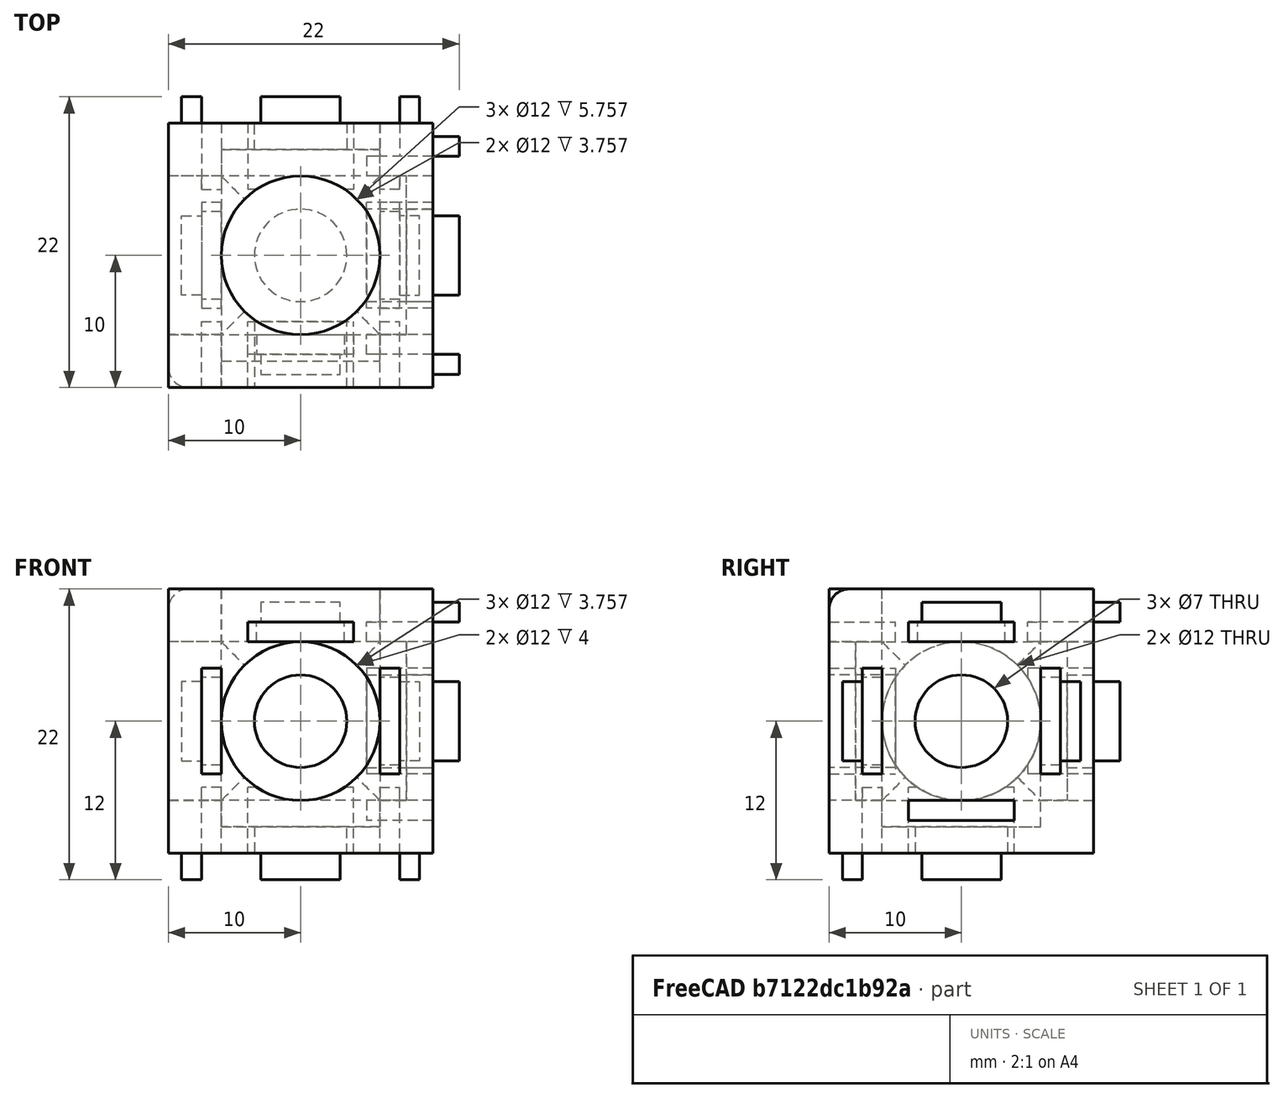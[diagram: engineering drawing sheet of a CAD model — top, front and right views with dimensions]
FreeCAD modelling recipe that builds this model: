
FCSTD DOCUMENT  (FreeCAD 0.15R4477 (Git))
Label: Wuerfelverbinder-20x20
License: CC-BY 3.0
LicenseURL: http://creativecommons.org/licenses/by/3.0/
objects: Sketcher::SketchObject×10, PartDesign::Pocket×6, PartDesign::Pad×4, PartDesign::Fillet×1
note: 31 computed .brp shape members not serialized (recipe doc carries the construction recipe); baked Part::Feature solids carry a one-line shape summary decoded from their .brp

FEATURE [Sketcher::SketchObject] Sketch
  Placement = pos=(0,0,0) rot=(1,0,0;1.5708rad)
  sketch-geometry (4):
    g0: LineSegment StartX=-10 StartY=10 StartZ=0 EndX=10 EndY=10 EndZ=0
    g1: LineSegment StartX=10 StartY=10 StartZ=0 EndX=10 EndY=-10 EndZ=0
    g2: LineSegment StartX=10 StartY=-10 StartZ=0 EndX=-10 EndY=-10 EndZ=0
    g3: LineSegment StartX=-10 StartY=-10 StartZ=0 EndX=-10 EndY=10 EndZ=0
  constraints (12):
    c: Coincident(g0,g1)
    c: Coincident(g1,g2)
    c: Coincident(g2,g3)
    c: Coincident(g3,g0)
    c: Horizontal(g0)
    c: Horizontal(g2)
    c: Vertical(g1)
    c: Vertical(g3)
    c: Symmetric(g0,g0,g-2)
    c: Symmetric(g2,g0,g-1)
    c: Distance(g0) = 20
    c: Distance(g1) = 20
FEATURE [PartDesign::Pad] Pad
  Length = 20
  Length2 = 100
  Midplane = true
  Placement = pos=(0,0,0) rot=(1,0,0;1.5708rad)
  Sketch = -> Sketch
  Type = 0
FEATURE [Sketcher::SketchObject] Sketch001
  Placement = pos=(0,-10,0) rot=(1,0,0;1.5708rad)
  Support = -> Pad [Face6]
  sketch-geometry (1):
    g0: Circle CenterX=0 CenterY=0 CenterZ=0 NormalX=0 NormalY=0 NormalZ=1 Radius=6
  constraints (2):
    c: Coincident(g0,g-1)
    c: Radius(g0) = 6
FEATURE [PartDesign::Pocket] Pocket
  Length = 18
  Placement = pos=(0,0,0) rot=(1,0,0;1.5708rad)
  Sketch = -> Sketch001
  Type = 0
FEATURE [Sketcher::SketchObject] Sketch003
  Placement = pos=(0,0,10) rot=(0,0,1;3.14159rad)
  Support = -> Pocket [Face1]
  sketch-geometry (1):
    g0: Circle CenterX=0 CenterY=0 CenterZ=0 NormalX=0 NormalY=0 NormalZ=1 Radius=6
  constraints (2):
    c: Coincident(g0,g-1)
    c: Radius(g0) = 6
FEATURE [PartDesign::Pocket] Pocket001
  Length = 18
  Placement = pos=(0,0,0) rot=(1,0,0;1.5708rad)
  Sketch = -> Sketch003
  Type = 0
FEATURE [Sketcher::SketchObject] Sketch004
  Placement = pos=(-10,0,0) rot=(0.707107,0,-0.707107;3.14159rad)
  Support = -> Pocket001 [Face2]
  sketch-geometry (1):
    g0: Circle CenterX=0 CenterY=0 CenterZ=0 NormalX=0 NormalY=0 NormalZ=1 Radius=6
  constraints (2):
    c: Coincident(g0,g-1)
    c: Radius(g0) = 6
FEATURE [PartDesign::Pocket] Pocket002
  Length = 18
  Placement = pos=(0,0,0) rot=(1,0,0;1.5708rad)
  Sketch = -> Sketch004
  Type = 0
FEATURE [Sketcher::SketchObject] Sketch005
  ExternalGeometry = -> [Pocket002]
  Placement = pos=(10,0,0) rot=(0.707107,0,0.707107;3.14159rad)
  Support = -> Pocket002 [Face5]
  sketch-geometry (12):
    g0: LineSegment StartX=7.5 StartY=3 StartZ=0 EndX=9 EndY=3 EndZ=0
    g1: LineSegment StartX=9 StartY=3 StartZ=0 EndX=9 EndY=-3 EndZ=0
    g2: LineSegment StartX=9 StartY=-3 StartZ=0 EndX=7.5 EndY=-3 EndZ=0
    g3: LineSegment StartX=7.5 StartY=-3 StartZ=0 EndX=7.5 EndY=3 EndZ=0
    g4: LineSegment StartX=3 StartY=9 StartZ=0 EndX=-3 EndY=9 EndZ=0
    g5: LineSegment StartX=-3 StartY=9 StartZ=0 EndX=-3 EndY=7.5 EndZ=0
    g6: LineSegment StartX=-3 StartY=7.5 StartZ=0 EndX=3 EndY=7.5 EndZ=0
    g7: LineSegment StartX=3 StartY=7.5 StartZ=0 EndX=3 EndY=9 EndZ=0
    g8: LineSegment StartX=3 StartY=-7.5 StartZ=0 EndX=-3 EndY=-7.5 EndZ=0
    g9: LineSegment StartX=-3 StartY=-7.5 StartZ=0 EndX=-3 EndY=-9 EndZ=0
    g10: LineSegment StartX=-3 StartY=-9 StartZ=0 EndX=3 EndY=-9 EndZ=0
    g11: LineSegment StartX=3 StartY=-9 StartZ=0 EndX=3 EndY=-7.5 EndZ=0
  constraints (36):
    c: Coincident(g0,g1)
    c: Coincident(g1,g2)
    c: Coincident(g2,g3)
    c: Coincident(g3,g0)
    c: Horizontal(g0)
    c: Horizontal(g2)
    c: Vertical(g1)
    c: Vertical(g3)
    c: Coincident(g4,g5)
    c: Coincident(g5,g6)
    c: Coincident(g6,g7)
    c: Coincident(g7,g4)
    c: Horizontal(g4)
    c: Horizontal(g6)
    c: Vertical(g5)
    c: Vertical(g7)
    c: Coincident(g8,g9)
    c: Coincident(g9,g10)
    c: Coincident(g10,g11)
    c: Coincident(g11,g8)
    c: Horizontal(g8)
    c: Horizontal(g10)
    c: Vertical(g9)
    c: Vertical(g11)
    c: Symmetric(g0,g1,g-1)
    c: Symmetric(g4,g4,g-2)
    c: Symmetric(g8,g8,g-2)
    c: Distance(g6) = 6
    c: Distance(g3) = 6
    c: Distance(g8) = 6
    c: Distance(g0,g-3) = 1
    c: Distance(g4,g-4) = 1
    c: Distance(g10,g-5) = 1
    c: Distance(g0) = 1.5
    c: Distance(g7) = 1.5
    c: Distance(g11) = 1.5
FEATURE [PartDesign::Pad] Pad001
  Length = 2
  Length2 = 100
  Placement = pos=(0,0,0) rot=(1,0,0;1.5708rad)
  Sketch = -> Sketch005
  Type = 0
FEATURE [Sketcher::SketchObject] Sketch006
  ExternalGeometry = -> [Pad001]
  Placement = pos=(10,0,0) rot=(0.707107,0,0.707107;3.14159rad)
  Support = -> Pad001 [Face5]
  sketch-geometry (13):
    g0: LineSegment StartX=-4 StartY=6 StartZ=0 EndX=4 EndY=6 EndZ=0
    g1: LineSegment StartX=4 StartY=6 StartZ=0 EndX=4 EndY=7.5 EndZ=0
    g2: LineSegment StartX=4 StartY=7.5 StartZ=0 EndX=-4 EndY=7.5 EndZ=0
    g3: LineSegment StartX=-4 StartY=7.5 StartZ=0 EndX=-4 EndY=6 EndZ=0
    g4: LineSegment StartX=6 StartY=4 StartZ=0 EndX=7.5 EndY=4 EndZ=0
    g5: LineSegment StartX=7.5 StartY=4 StartZ=0 EndX=7.5 EndY=-4 EndZ=0
    g6: LineSegment StartX=7.5 StartY=-4 StartZ=0 EndX=6 EndY=-4 EndZ=0
    g7: LineSegment StartX=6 StartY=-4 StartZ=0 EndX=6 EndY=4 EndZ=0
    g8: LineSegment StartX=-4 StartY=-6 StartZ=0 EndX=4 EndY=-6 EndZ=0
    g9: LineSegment StartX=4 StartY=-6 StartZ=0 EndX=4 EndY=-7.5 EndZ=0
    g10: LineSegment StartX=4 StartY=-7.5 StartZ=0 EndX=-4 EndY=-7.5 EndZ=0
    g11: LineSegment StartX=-4 StartY=-7.5 StartZ=0 EndX=-4 EndY=-6 EndZ=0
    g12: Circle CenterX=0 CenterY=0 CenterZ=0 NormalX=0 NormalY=0 NormalZ=1 Radius=3.5
  constraints (38):
    c: Coincident(g0,g1)
    c: Coincident(g1,g2)
    c: Coincident(g2,g3)
    c: Coincident(g3,g0)
    c: Horizontal(g0)
    c: Horizontal(g2)
    c: Vertical(g1)
    c: Vertical(g3)
    c: Coincident(g4,g5)
    c: Coincident(g5,g6)
    c: Coincident(g6,g7)
    c: Coincident(g7,g4)
    c: Horizontal(g4)
    c: Horizontal(g6)
    c: Vertical(g5)
    c: Vertical(g7)
    c: Coincident(g8,g9)
    c: Coincident(g9,g10)
    c: Coincident(g10,g11)
    c: Coincident(g11,g8)
    c: Horizontal(g8)
    c: Horizontal(g10)
    c: Vertical(g9)
    c: Vertical(g11)
    c: Symmetric(g2,g1,g-2)
    c: Symmetric(g4,g6,g-1)
    c: Symmetric(g8,g8,g-2)
    c: Distance(g3) = 1.5
    c: Distance(g4) = 1.5
    c: Distance(g11) = 1.5
    c: Distance(g8) = 8
    c: Distance(g7) = 8
    c: Distance(g0) = 8
    c: PointOnObject(g-5,g10)
    c: PointOnObject(g-4,g5)
    c: PointOnObject(g-3,g2)
    c: Coincident(g12,g-1)
    c: Radius(g12) = 3.5
FEATURE [PartDesign::Pocket] Pocket003
  Length = 5
  Placement = pos=(0,0,0) rot=(1,0,0;1.5708rad)
  Sketch = -> Sketch006
  Type = 0
FEATURE [Sketcher::SketchObject] Sketch007
  ExternalGeometry = -> [Pocket003]
  Placement = pos=(0,0,-10) rot=(1,0,0;3.14159rad)
  Support = -> Pocket003 [Face7]
  sketch-geometry (12):
    g0: LineSegment StartX=-3 StartY=9 StartZ=0 EndX=3 EndY=9 EndZ=0
    g1: LineSegment StartX=3 StartY=9 StartZ=0 EndX=3 EndY=7.5 EndZ=0
    g2: LineSegment StartX=3 StartY=7.5 StartZ=0 EndX=-3 EndY=7.5 EndZ=0
    g3: LineSegment StartX=-3 StartY=7.5 StartZ=0 EndX=-3 EndY=9 EndZ=0
    g4: LineSegment StartX=-7.5 StartY=3 StartZ=0 EndX=-9 EndY=3 EndZ=0
    g5: LineSegment StartX=-9 StartY=3 StartZ=0 EndX=-9 EndY=-3 EndZ=0
    g6: LineSegment StartX=-9 StartY=-3 StartZ=0 EndX=-7.5 EndY=-3 EndZ=0
    g7: LineSegment StartX=-7.5 StartY=-3 StartZ=0 EndX=-7.5 EndY=3 EndZ=0
    g8: LineSegment StartX=7.5 StartY=3 StartZ=0 EndX=9 EndY=3 EndZ=0
    g9: LineSegment StartX=9 StartY=3 StartZ=0 EndX=9 EndY=-3 EndZ=0
    g10: LineSegment StartX=9 StartY=-3 StartZ=0 EndX=7.5 EndY=-3 EndZ=0
    g11: LineSegment StartX=7.5 StartY=-3 StartZ=0 EndX=7.5 EndY=3 EndZ=0
  constraints (36):
    c: Coincident(g0,g1)
    c: Coincident(g1,g2)
    c: Coincident(g2,g3)
    c: Coincident(g3,g0)
    c: Horizontal(g0)
    c: Horizontal(g2)
    c: Vertical(g1)
    c: Vertical(g3)
    c: Coincident(g4,g5)
    c: Coincident(g5,g6)
    c: Coincident(g6,g7)
    c: Coincident(g7,g4)
    c: Horizontal(g4)
    c: Horizontal(g6)
    c: Vertical(g5)
    c: Vertical(g7)
    c: Coincident(g8,g9)
    c: Coincident(g9,g10)
    c: Coincident(g10,g11)
    c: Coincident(g11,g8)
    c: Horizontal(g8)
    c: Horizontal(g10)
    c: Vertical(g9)
    c: Vertical(g11)
    c: Symmetric(g0,g0,g-2)
    c: Symmetric(g4,g5,g-1)
    c: Symmetric(g8,g10,g-1)
    c: Distance(g3) = 1.5
    c: Distance(g8) = 1.5
    c: Distance(g4) = 1.5
    c: Distance(g0,g-3) = 1
    c: Distance(g8,g-5) = 1
    c: Distance(g4,g-4) = 1
    c: Distance(g2) = 6
    c: Distance(g11) = 6
    c: Distance(g7) = 6
FEATURE [PartDesign::Pad] Pad002
  Length = 2
  Length2 = 100
  Placement = pos=(0,0,0) rot=(1,0,0;1.5708rad)
  Sketch = -> Sketch007
  Type = 0
FEATURE [Sketcher::SketchObject] Sketch008
  ExternalGeometry = -> [Pad002]
  Placement = pos=(0,0,-10) rot=(1,0,0;3.14159rad)
  Support = -> Pad002 [Face7]
  sketch-geometry (13):
    g0: LineSegment StartX=-4 StartY=6 StartZ=0 EndX=4 EndY=6 EndZ=0
    g1: LineSegment StartX=4 StartY=6 StartZ=0 EndX=4 EndY=7.5 EndZ=0
    g2: LineSegment StartX=4 StartY=7.5 StartZ=0 EndX=-4 EndY=7.5 EndZ=0
    g3: LineSegment StartX=-4 StartY=7.5 StartZ=0 EndX=-4 EndY=6 EndZ=0
    g4: LineSegment StartX=6 StartY=4 StartZ=0 EndX=7.5 EndY=4 EndZ=0
    g5: LineSegment StartX=7.5 StartY=4 StartZ=0 EndX=7.5 EndY=-4 EndZ=0
    g6: LineSegment StartX=7.5 StartY=-4 StartZ=0 EndX=6 EndY=-4 EndZ=0
    g7: LineSegment StartX=6 StartY=-4 StartZ=0 EndX=6 EndY=4 EndZ=0
    g8: LineSegment StartX=-7.5 StartY=4 StartZ=0 EndX=-6 EndY=4 EndZ=0
    g9: LineSegment StartX=-6 StartY=4 StartZ=0 EndX=-6 EndY=-4 EndZ=0
    g10: LineSegment StartX=-6 StartY=-4 StartZ=0 EndX=-7.5 EndY=-4 EndZ=0
    g11: LineSegment StartX=-7.5 StartY=-4 StartZ=0 EndX=-7.5 EndY=4 EndZ=0
    g12: Circle CenterX=0 CenterY=0 CenterZ=0 NormalX=0 NormalY=0 NormalZ=1 Radius=3.5
  constraints (38):
    c: Coincident(g0,g1)
    c: Coincident(g1,g2)
    c: Coincident(g2,g3)
    c: Coincident(g3,g0)
    c: Horizontal(g0)
    c: Horizontal(g2)
    c: Vertical(g1)
    c: Vertical(g3)
    c: Coincident(g4,g5)
    c: Coincident(g5,g6)
    c: Coincident(g6,g7)
    c: Coincident(g7,g4)
    c: Horizontal(g4)
    c: Horizontal(g6)
    c: Vertical(g5)
    c: Vertical(g7)
    c: Coincident(g8,g9)
    c: Coincident(g9,g10)
    c: Coincident(g10,g11)
    c: Coincident(g11,g8)
    c: Horizontal(g8)
    c: Horizontal(g10)
    c: Vertical(g9)
    c: Vertical(g11)
    c: Symmetric(g8,g10,g-1)
    c: Symmetric(g2,g1,g-2)
    c: Symmetric(g4,g6,g-1)
    c: Distance(g2) = 8
    c: Distance(g9) = 8
    c: Distance(g7) = 8
    c: Distance(g3) = 1.5
    c: Distance(g8) = 1.5
    c: Distance(g4) = 1.5
    c: PointOnObject(g-3,g2)
    c: PointOnObject(g-4,g5)
    c: PointOnObject(g-5,g11)
    c: Coincident(g12,g-1)
    c: Radius(g12) = 3.5
FEATURE [PartDesign::Pocket] Pocket004
  Length = 5
  Placement = pos=(0,0,0) rot=(1,0,0;1.5708rad)
  Sketch = -> Sketch008
  Type = 0
FEATURE [Sketcher::SketchObject] Sketch009
  ExternalGeometry = -> [Pocket004]
  Placement = pos=(0,10,0) rot=(-1,0,0;1.5708rad)
  Support = -> Pocket004 [Face3]
  sketch-geometry (12):
    g0: LineSegment StartX=3 StartY=-9 StartZ=0 EndX=-3 EndY=-9 EndZ=0
    g1: LineSegment StartX=-3 StartY=-9 StartZ=0 EndX=-3 EndY=-7.5 EndZ=0
    g2: LineSegment StartX=-3 StartY=-7.5 StartZ=0 EndX=3 EndY=-7.5 EndZ=0
    g3: LineSegment StartX=3 StartY=-7.5 StartZ=0 EndX=3 EndY=-9 EndZ=0
    g4: LineSegment StartX=-7.5 StartY=-3 StartZ=0 EndX=-9 EndY=-3 EndZ=0
    g5: LineSegment StartX=-9 StartY=-3 StartZ=0 EndX=-9 EndY=3 EndZ=0
    g6: LineSegment StartX=-9 StartY=3 StartZ=0 EndX=-7.5 EndY=3 EndZ=0
    g7: LineSegment StartX=-7.5 StartY=3 StartZ=0 EndX=-7.5 EndY=-3 EndZ=0
    g8: LineSegment StartX=7.5 StartY=-3 StartZ=0 EndX=9 EndY=-3 EndZ=0
    g9: LineSegment StartX=9 StartY=-3 StartZ=0 EndX=9 EndY=3 EndZ=0
    g10: LineSegment StartX=9 StartY=3 StartZ=0 EndX=7.5 EndY=3 EndZ=0
    g11: LineSegment StartX=7.5 StartY=3 StartZ=0 EndX=7.5 EndY=-3 EndZ=0
  constraints (36):
    c: Coincident(g0,g1)
    c: Coincident(g1,g2)
    c: Coincident(g2,g3)
    c: Coincident(g3,g0)
    c: Horizontal(g0)
    c: Horizontal(g2)
    c: Vertical(g1)
    c: Vertical(g3)
    c: Coincident(g4,g5)
    c: Coincident(g5,g6)
    c: Coincident(g6,g7)
    c: Coincident(g7,g4)
    c: Horizontal(g4)
    c: Horizontal(g6)
    c: Vertical(g5)
    c: Vertical(g7)
    c: Coincident(g8,g9)
    c: Coincident(g9,g10)
    c: Coincident(g10,g11)
    c: Coincident(g11,g8)
    c: Horizontal(g8)
    c: Horizontal(g10)
    c: Vertical(g9)
    c: Vertical(g11)
    c: Symmetric(g0,g0,g-2)
    c: Symmetric(g8,g9,g-1)
    c: Symmetric(g4,g6,g-1)
    c: Distance(g2) = 6
    c: Distance(g11) = 6
    c: Distance(g7) = 6
    c: Distance(g1) = 1.5
    c: Distance(g8) = 1.5
    c: Distance(g4) = 1.5
    c: Distance(g0,g-3) = 1
    c: Distance(g4,g-4) = 1
    c: Distance(g8,g-5) = 1
FEATURE [PartDesign::Pad] Pad003
  Length = 2
  Length2 = 100
  Placement = pos=(0,0,0) rot=(1,0,0;1.5708rad)
  Sketch = -> Sketch009
  Type = 0
FEATURE [Sketcher::SketchObject] Sketch010
  ExternalGeometry = -> [Pad003]
  Placement = pos=(0,10,0) rot=(-1,0,0;1.5708rad)
  Support = -> Pad003 [Face3]
  sketch-geometry (13):
    g0: LineSegment StartX=-7.5 StartY=4 StartZ=0 EndX=-6 EndY=4 EndZ=0
    g1: LineSegment StartX=-6 StartY=4 StartZ=0 EndX=-6 EndY=-4 EndZ=0
    g2: LineSegment StartX=-6 StartY=-4 StartZ=0 EndX=-7.5 EndY=-4 EndZ=0
    g3: LineSegment StartX=-7.5 StartY=-4 StartZ=0 EndX=-7.5 EndY=4 EndZ=0
    g4: LineSegment StartX=6 StartY=4 StartZ=0 EndX=7.5 EndY=4 EndZ=0
    g5: LineSegment StartX=7.5 StartY=4 StartZ=0 EndX=7.5 EndY=-4 EndZ=0
    g6: LineSegment StartX=7.5 StartY=-4 StartZ=0 EndX=6 EndY=-4 EndZ=0
    g7: LineSegment StartX=6 StartY=-4 StartZ=0 EndX=6 EndY=4 EndZ=0
    g8: LineSegment StartX=-4 StartY=-6 StartZ=0 EndX=4 EndY=-6 EndZ=0
    g9: LineSegment StartX=4 StartY=-6 StartZ=0 EndX=4 EndY=-7.5 EndZ=0
    g10: LineSegment StartX=4 StartY=-7.5 StartZ=0 EndX=-4 EndY=-7.5 EndZ=0
    g11: LineSegment StartX=-4 StartY=-7.5 StartZ=0 EndX=-4 EndY=-6 EndZ=0
    g12: Circle CenterX=0 CenterY=0 CenterZ=0 NormalX=0 NormalY=0 NormalZ=1 Radius=3.5
  constraints (38):
    c: Coincident(g0,g1)
    c: Coincident(g1,g2)
    c: Coincident(g2,g3)
    c: Coincident(g3,g0)
    c: Horizontal(g0)
    c: Horizontal(g2)
    c: Vertical(g1)
    c: Vertical(g3)
    c: Coincident(g4,g5)
    c: Coincident(g5,g6)
    c: Coincident(g6,g7)
    c: Coincident(g7,g4)
    c: Horizontal(g4)
    c: Horizontal(g6)
    c: Vertical(g5)
    c: Vertical(g7)
    c: Coincident(g8,g9)
    c: Coincident(g9,g10)
    c: Coincident(g10,g11)
    c: Coincident(g11,g8)
    c: Horizontal(g8)
    c: Horizontal(g10)
    c: Vertical(g9)
    c: Vertical(g11)
    c: Symmetric(g0,g2,g-1)
    c: Symmetric(g4,g6,g-1)
    c: Symmetric(g8,g8,g-2)
    c: Distance(g1) = 8
    c: Distance(g7) = 8
    c: Distance(g8) = 8
    c: Distance(g0) = 1.5
    c: Distance(g4) = 1.5
    c: Distance(g9) = 1.5
    c: PointOnObject(g-3,g3)
    c: PointOnObject(g-5,g10)
    c: PointOnObject(g-4,g5)
    c: Coincident(g12,g-1)
    c: Radius(g12) = 3.5
FEATURE [PartDesign::Pocket] Pocket005
  Length = 5
  Placement = pos=(0,0,0) rot=(1,0,0;1.5708rad)
  Sketch = -> Sketch010
  Type = 0
FEATURE [PartDesign::Fillet] Fillet
  Base = -> Pocket005 [Edge1,Edge3,Edge8]
  Placement = pos=(0,0,0) rot=(1,0,0;1.5708rad)
  Radius = 1.5
